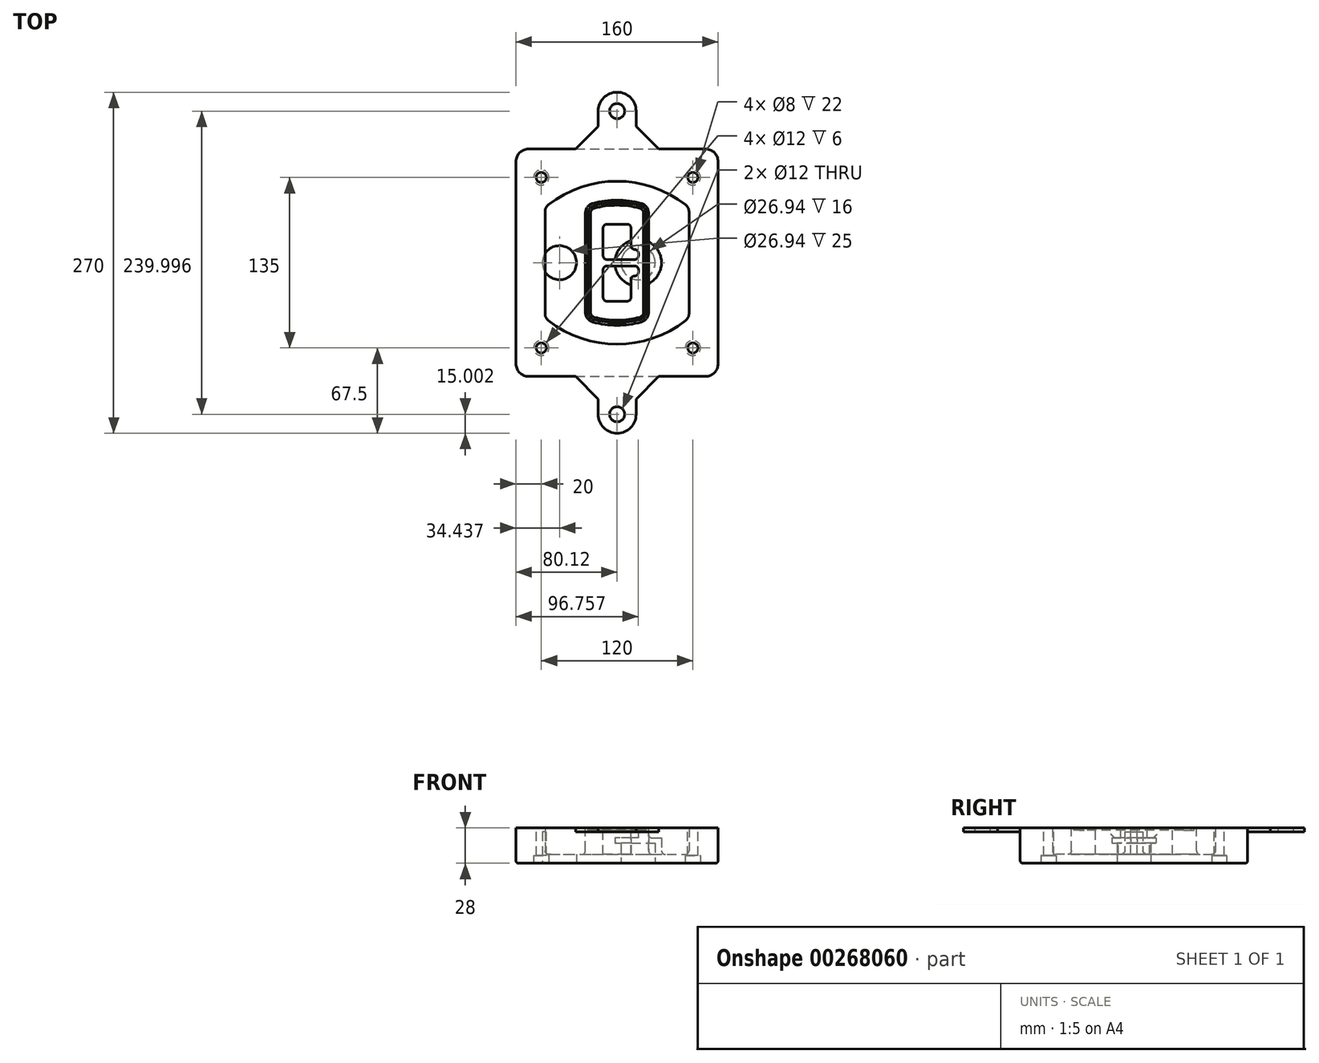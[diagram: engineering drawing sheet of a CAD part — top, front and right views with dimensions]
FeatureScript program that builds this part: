
annotation { "Feature Type Name" : "Feature", "Feature Type Description" : "" }
export const myFeature = defineFeature(function(context is Context, id is Id, definition is map)
    precondition{}
    {
        {
            var Q0;
            Q0=qCreatedBy(makeId("Top.planeOp"),FACE);
            var sketch = newSketch(context, id + "F0", { "sketchPlane" : qUnion([Q0])});
            skPoint(sketch, "E0.rect.middle", {"position": v(0, 0) * mm});
            skLineSegment(sketch, "E1.bottom", {"start": v(-70, -90) * mm, "end": v(70, -90) * mm});
            skLineSegment(sketch, "E1.top", {"start": v(-70, 90) * mm, "end": v(70, 90) * mm});
            skLineSegment(sketch, "E1.left", {"start": v(-80, -80) * mm, "end": v(-80, 80) * mm});
            skLineSegment(sketch, "E1.right", {"start": v(80, -80) * mm, "end": v(80, 80) * mm});
            skLineSegment(sketch, "E2", {"start": v(-80, 90) * mm, "end": v(80, -90) * mm, "construction": true});
            skLineSegment(sketch, "E3", {"start": v(80, 90) * mm, "end": v(-80, -90) * mm, "construction": true});
            skCircle(sketch, "E4", {"center": v(-60, 67.5) * mm, "radius": 4 * mm});
            skCircle(sketch, "E5", {"center": v(60, 67.5) * mm, "radius": 4 * mm});
            skCircle(sketch, "E6", {"center": v(60, -67.5) * mm, "radius": 4 * mm});
            skCircle(sketch, "E7", {"center": v(-60, -67.5) * mm, "radius": 4 * mm});
            skLineSegment(sketch, "E8", {"start": v(-60, 67.5) * mm, "end": v(60, 67.5) * mm, "construction": true});
            skLineSegment(sketch, "E9", {"start": v(60, 67.5) * mm, "end": v(60, -67.5) * mm, "construction": true});
            skLineSegment(sketch, "E10", {"start": v(60, -67.5) * mm, "end": v(-60, -67.5) * mm, "construction": true});
            skLineSegment(sketch, "E11", {"start": v(-60, -67.5) * mm, "end": v(-60, 67.5) * mm, "construction": true});
            skLineSegment(sketch, "E12", {"start": v(-60, 40.3) * mm, "end": v(-60, -40.3) * mm});
            skLineSegment(sketch, "E13", {"start": v(60, 40.3) * mm, "end": v(60, -40.3) * mm});
            skArc(sketch, "E14", {"start": v(56.15, 48.18) * mm, "mid": v(0, 67.5) * mm, "end": v(-56.15, 48.18) * mm});
            skArc(sketch, "E15", {"start": v(-56.15, -48.18) * mm, "mid": v(0, -67.5) * mm, "end": v(56.15, -48.18) * mm});
            skLineSegment(sketch, "E16", {"start": v(-60, 0) * mm, "end": v(60, 0) * mm, "construction": true});
            skPoint(sketch, "E17.visualSharp", {"position": v(-60, -45) * mm});
            skArc(sketch, "E17.filletArc", {"start": v(-60, -40.3) * mm, "mid": v(-58.99, -44.68) * mm, "end": v(-56.15, -48.18) * mm});
            skPoint(sketch, "E18.visualSharp", {"position": v(-60, 45) * mm});
            skArc(sketch, "E18.filletArc", {"start": v(-56.15, 48.18) * mm, "mid": v(-58.99, 44.68) * mm, "end": v(-60, 40.3) * mm});
            skPoint(sketch, "E19.visualSharp", {"position": v(60, 45) * mm});
            skArc(sketch, "E19.filletArc", {"start": v(60, 40.3) * mm, "mid": v(58.99, 44.68) * mm, "end": v(56.15, 48.18) * mm});
            skPoint(sketch, "E20.visualSharp", {"position": v(60, -45) * mm});
            skArc(sketch, "E20.filletArc", {"start": v(56.15, -48.18) * mm, "mid": v(58.99, -44.68) * mm, "end": v(60, -40.3) * mm});
            skPoint(sketch, "E21.visualSharp", {"position": v(-80, 90) * mm});
            skArc(sketch, "E21.filletArc", {"start": v(-70, 90) * mm, "mid": v(-77.07, 87.07) * mm, "end": v(-80, 80) * mm});
            skPoint(sketch, "E22.visualSharp", {"position": v(80, 90) * mm});
            skArc(sketch, "E22.filletArc", {"start": v(80, 80) * mm, "mid": v(77.07, 87.07) * mm, "end": v(70, 90) * mm});
            skPoint(sketch, "E23.visualSharp", {"position": v(80, -90) * mm});
            skArc(sketch, "E23.filletArc", {"start": v(70, -90) * mm, "mid": v(77.07, -87.07) * mm, "end": v(80, -80) * mm});
            skPoint(sketch, "E24.visualSharp", {"position": v(-80, -90) * mm});
            skArc(sketch, "E24.filletArc", {"start": v(-80, -80) * mm, "mid": v(-77.07, -87.07) * mm, "end": v(-70, -90) * mm});
            skArc(sketch, "E25.0", {"start": v(57, 40.3) * mm, "mid": v(56.3, 43.36) * mm, "end": v(54.3, 45.81) * mm});
            skLineSegment(sketch, "E25.1", {"start": v(57, 40.3) * mm, "end": v(57, -40.3) * mm});
            skArc(sketch, "E25.2", {"start": v(54.3, -45.81) * mm, "mid": v(56.3, -43.36) * mm, "end": v(57, -40.3) * mm});
            skArc(sketch, "E25.3", {"start": v(-54.3, -45.81) * mm, "mid": v(0, -64.5) * mm, "end": v(54.3, -45.81) * mm});
            skArc(sketch, "E25.4", {"start": v(-57, -40.3) * mm, "mid": v(-56.3, -43.36) * mm, "end": v(-54.3, -45.81) * mm});
            skArc(sketch, "E25.5", {"start": v(54.3, 45.81) * mm, "mid": v(0, 64.5) * mm, "end": v(-54.3, 45.81) * mm});
            skLineSegment(sketch, "E25.6", {"start": v(-57, 40.3) * mm, "end": v(-57, -40.3) * mm});
            skArc(sketch, "E25.7", {"start": v(-54.3, 45.81) * mm, "mid": v(-56.3, 43.36) * mm, "end": v(-57, 40.3) * mm});
            skArc(sketch, "E26.0", {"start": v(-58.62, 51.33) * mm, "mid": v(-62.58, 46.43) * mm, "end": v(-64, 40.3) * mm});
            skArc(sketch, "E26.1", {"start": v(58.62, 51.33) * mm, "mid": v(0, 71.5) * mm, "end": v(-58.62, 51.33) * mm});
            skArc(sketch, "E26.2", {"start": v(64, 40.3) * mm, "mid": v(62.58, 46.43) * mm, "end": v(58.62, 51.33) * mm});
            skLineSegment(sketch, "E26.3", {"start": v(64, 40.3) * mm, "end": v(64, -40.3) * mm});
            skArc(sketch, "E26.4", {"start": v(58.62, -51.33) * mm, "mid": v(62.58, -46.43) * mm, "end": v(64, -40.3) * mm});
            skLineSegment(sketch, "E26.5", {"start": v(-64, 40.3) * mm, "end": v(-64, -40.3) * mm});
            skArc(sketch, "E26.6", {"start": v(-58.62, -51.33) * mm, "mid": v(0, -71.5) * mm, "end": v(58.62, -51.33) * mm});
            skArc(sketch, "E26.7", {"start": v(-64, -40.3) * mm, "mid": v(-62.58, -46.43) * mm, "end": v(-58.62, -51.33) * mm});
            skSolve(sketch);
        }
        {
            var Q0;
            Q0=makeQuery(id+"F0.imprint","IMPRINT",FACE,{"disambiguationData":[TD([[makeQuery(id+"F0.imprint","IMPRINT",EDGE,{"derivedFrom":sQuery(id+"F0.wireOp",EDGE,"E1.bottom")}),1.0]])]});
            var Q1;
            Q1=makeQuery(id+"F0.imprint","IMPRINT",FACE,{"disambiguationData":[TD([[makeQuery(id+"F0.imprint","IMPRINT",EDGE,{"derivedFrom":sQuery(id+"F0.wireOp",EDGE,"E12")}),1.0]])]});
            var Q2;
            Q2=makeQuery(id+"F0.imprint","IMPRINT",FACE,{"disambiguationData":[TD([[makeQuery(id+"F0.imprint","IMPRINT",EDGE,{"derivedFrom":sQuery(id+"F0.wireOp",EDGE,"E25.0")}),1.0]])]});
            var Q3;
            Q3=makeQuery(id+"F0.imprint","IMPRINT",FACE,{"disambiguationData":[TD([[makeQuery(id+"F0.imprint","IMPRINT",EDGE,{"derivedFrom":sQuery(id+"F0.wireOp",EDGE,"E12")}),-1.0]])]});
            extrude(context, id + "F1", {"entities" : qUnion([Q0, Q1, Q2, Q3]), "oppositeDirection" : true, "depth" : 25 * mm});
        }
        {
            var Q0;
            Q0=makeQuery(id+"F0.imprint","IMPRINT",FACE,{"disambiguationData":[TD([[makeQuery(id+"F0.imprint","IMPRINT",EDGE,{"derivedFrom":sQuery(id+"F0.wireOp",EDGE,"E12")}),1.0]])]});
            extrude(context, id + "F2", {"entities" : qUnion([Q0]), "operationType" : NewBodyOperationType.ADD, "depth" : 3 * mm});
        }
        {
            var Q0;
            Q0=makeQuery(id+"F0.imprint","IMPRINT",FACE,{"disambiguationData":[TD([[makeQuery(id+"F0.imprint","IMPRINT",EDGE,{"derivedFrom":sQuery(id+"F0.wireOp",EDGE,"E25.0")}),1.0]])]});
            extrude(context, id + "F3", {"entities" : qUnion([Q0]), "operationType" : NewBodyOperationType.REMOVE, "oppositeDirection" : true, "depth" : 18 * mm});
        }
        {
            var Q0;
            Q0=makeQuery(id+"F2.opExtrude","CAP_FACE",FACE,{"disambiguationData":[OSD([sQuery(id+"F0.wireOp",EDGE,"E12"),sQuery(id+"F0.wireOp",EDGE,"E13"),sQuery(id+"F0.wireOp",EDGE,"E14"),sQuery(id+"F0.wireOp",EDGE,"E15"),sQuery(id+"F0.wireOp",EDGE,"E17.filletArc"),sQuery(id+"F0.wireOp",EDGE,"E18.filletArc"),sQuery(id+"F0.wireOp",EDGE,"E19.filletArc"),sQuery(id+"F0.wireOp",EDGE,"E20.filletArc"),sQuery(id+"F0.wireOp",EDGE,"E25.0"),sQuery(id+"F0.wireOp",EDGE,"E25.1"),sQuery(id+"F0.wireOp",EDGE,"E25.2"),sQuery(id+"F0.wireOp",EDGE,"E25.3"),sQuery(id+"F0.wireOp",EDGE,"E25.4"),sQuery(id+"F0.wireOp",EDGE,"E25.5"),sQuery(id+"F0.wireOp",EDGE,"E25.6"),sQuery(id+"F0.wireOp",EDGE,"E25.7")])],"isStart":false});
            var sketch = newSketch(context, id + "F4", { "sketchPlane" : qUnion([Q0])});
            skArc(sketch, "E27.0", {"start": v(-19.08, -46.97) * mm, "mid": v(0, -49.5) * mm, "end": v(19.08, -46.97) * mm});
            skArc(sketch, "E28.0", {"start": v(19.08, 46.97) * mm, "mid": v(0, 49.5) * mm, "end": v(-19.08, 46.97) * mm});
            skLineSegment(sketch, "E29", {"start": v(-25, 39.25) * mm, "end": v(-25, -39.25) * mm});
            skLineSegment(sketch, "E30", {"start": v(25, 39.25) * mm, "end": v(25, -39.25) * mm});
            skLineSegment(sketch, "E31", {"start": v(-25, 45.1) * mm, "end": v(25, 45.1) * mm, "construction": true});
            skLineSegment(sketch, "E32", {"start": v(-25, -45.1) * mm, "end": v(25, -45.1) * mm, "construction": true});
            skPoint(sketch, "E33.visualSharp", {"position": v(-25, 45.1) * mm});
            skArc(sketch, "E33.filletArc", {"start": v(-19.08, 46.97) * mm, "mid": v(-23.35, 44.11) * mm, "end": v(-25, 39.25) * mm});
            skPoint(sketch, "E34.visualSharp", {"position": v(25, 45.1) * mm});
            skArc(sketch, "E34.filletArc", {"start": v(25, 39.25) * mm, "mid": v(23.35, 44.11) * mm, "end": v(19.08, 46.97) * mm});
            skPoint(sketch, "E35.visualSharp", {"position": v(25, -45.1) * mm});
            skArc(sketch, "E35.filletArc", {"start": v(19.08, -46.97) * mm, "mid": v(23.35, -44.11) * mm, "end": v(25, -39.25) * mm});
            skPoint(sketch, "E36.visualSharp", {"position": v(-25, -45.1) * mm});
            skArc(sketch, "E36.filletArc", {"start": v(-25, -39.25) * mm, "mid": v(-23.35, -44.11) * mm, "end": v(-19.08, -46.97) * mm});
            skArc(sketch, "E37.0", {"start": v(54.3, 45.81) * mm, "mid": v(0, 64.5) * mm, "end": v(-54.3, 45.81) * mm});
            skArc(sketch, "E37.1", {"start": v(-54.3, 45.81) * mm, "mid": v(-56.3, 43.36) * mm, "end": v(-57, 40.3) * mm});
            skLineSegment(sketch, "E37.2", {"start": v(-57, 40.3) * mm, "end": v(-57, -40.3) * mm});
            skArc(sketch, "E37.3", {"start": v(-57, -40.3) * mm, "mid": v(-56.3, -43.36) * mm, "end": v(-54.3, -45.81) * mm});
            skArc(sketch, "E37.4", {"start": v(-54.3, -45.81) * mm, "mid": v(0, -64.5) * mm, "end": v(54.3, -45.81) * mm});
            skArc(sketch, "E37.5", {"start": v(54.3, -45.81) * mm, "mid": v(56.3, -43.36) * mm, "end": v(57, -40.3) * mm});
            skLineSegment(sketch, "E37.6", {"start": v(57, 40.3) * mm, "end": v(57, -40.3) * mm});
            skArc(sketch, "E37.7", {"start": v(57, 40.3) * mm, "mid": v(56.3, 43.36) * mm, "end": v(54.3, 45.81) * mm});
            skLineSegment(sketch, "E38.0", {"start": v(23, 39.25) * mm, "end": v(23, -39.25) * mm});
            skArc(sketch, "E38.1", {"start": v(18.56, -45.04) * mm, "mid": v(21.76, -42.9) * mm, "end": v(23, -39.25) * mm});
            skArc(sketch, "E38.2", {"start": v(-18.56, -45.04) * mm, "mid": v(0, -47.5) * mm, "end": v(18.56, -45.04) * mm});
            skArc(sketch, "E38.3", {"start": v(-23, -39.25) * mm, "mid": v(-21.76, -42.9) * mm, "end": v(-18.56, -45.04) * mm});
            skLineSegment(sketch, "E38.4", {"start": v(-23, 39.25) * mm, "end": v(-23, -39.25) * mm});
            skArc(sketch, "E38.5", {"start": v(23, 39.25) * mm, "mid": v(21.76, 42.9) * mm, "end": v(18.56, 45.04) * mm});
            skArc(sketch, "E38.6", {"start": v(-18.56, 45.04) * mm, "mid": v(-21.76, 42.9) * mm, "end": v(-23, 39.25) * mm});
            skArc(sketch, "E38.7", {"start": v(18.56, 45.04) * mm, "mid": v(0, 47.5) * mm, "end": v(-18.56, 45.04) * mm});
            skArc(sketch, "E39.0", {"start": v(21, 39.25) * mm, "mid": v(20.18, 41.68) * mm, "end": v(18.04, 43.1) * mm});
            skLineSegment(sketch, "E39.1", {"start": v(21, 39.25) * mm, "end": v(21, -39.25) * mm});
            skArc(sketch, "E39.2", {"start": v(18.04, -43.1) * mm, "mid": v(20.18, -41.68) * mm, "end": v(21, -39.25) * mm});
            skArc(sketch, "E39.3", {"start": v(-18.04, -43.1) * mm, "mid": v(0, -45.5) * mm, "end": v(18.04, -43.1) * mm});
            skArc(sketch, "E39.4", {"start": v(-21, -39.25) * mm, "mid": v(-20.18, -41.68) * mm, "end": v(-18.04, -43.1) * mm});
            skArc(sketch, "E39.5", {"start": v(18.04, 43.1) * mm, "mid": v(0, 45.5) * mm, "end": v(-18.04, 43.1) * mm});
            skLineSegment(sketch, "E39.6", {"start": v(-21, 39.25) * mm, "end": v(-21, -39.25) * mm});
            skArc(sketch, "E39.7", {"start": v(-18.04, 43.1) * mm, "mid": v(-20.18, 41.68) * mm, "end": v(-21, 39.25) * mm});
            skLineSegment(sketch, "E40", {"start": v(-25, 0) * mm, "end": v(25, 0) * mm, "construction": true});
            skLineSegment(sketch, "E41", {"start": v(-11, 5.5) * mm, "end": v(-11, 27.5) * mm});
            skLineSegment(sketch, "E42", {"start": v(-8, 30.5) * mm, "end": v(8, 30.5) * mm});
            skLineSegment(sketch, "E43", {"start": v(11, 27.5) * mm, "end": v(11, 13.5) * mm});
            skLineSegment(sketch, "E44", {"start": v(14, 10.5) * mm, "end": v(14, 10.5) * mm});
            skLineSegment(sketch, "E45", {"start": v(17, 7.5) * mm, "end": v(17, 5.5) * mm});
            skLineSegment(sketch, "E46", {"start": v(14, 2.5) * mm, "end": v(-8, 2.5) * mm});
            skPoint(sketch, "E47.visualSharp", {"position": v(-11, 30.5) * mm});
            skArc(sketch, "E47.filletArc", {"start": v(-8, 30.5) * mm, "mid": v(-10.12, 29.62) * mm, "end": v(-11, 27.5) * mm});
            skPoint(sketch, "E48.visualSharp", {"position": v(11, 30.5) * mm});
            skArc(sketch, "E48.filletArc", {"start": v(11, 27.5) * mm, "mid": v(10.12, 29.62) * mm, "end": v(8, 30.5) * mm});
            skPoint(sketch, "E49.visualSharp", {"position": v(11, 10.5) * mm});
            skArc(sketch, "E49.filletArc", {"start": v(11, 13.5) * mm, "mid": v(11.88, 11.38) * mm, "end": v(14, 10.5) * mm});
            skPoint(sketch, "E50.visualSharp", {"position": v(17, 10.5) * mm});
            skArc(sketch, "E50.filletArc", {"start": v(17, 7.5) * mm, "mid": v(16.12, 9.62) * mm, "end": v(14, 10.5) * mm});
            skPoint(sketch, "E51.visualSharp", {"position": v(17, 2.5) * mm});
            skArc(sketch, "E51.filletArc", {"start": v(14, 2.5) * mm, "mid": v(16.12, 3.38) * mm, "end": v(17, 5.5) * mm});
            skPoint(sketch, "E52.visualSharp", {"position": v(-11, 2.5) * mm});
            skArc(sketch, "E52.filletArc", {"start": v(-11, 5.5) * mm, "mid": v(-10.12, 3.38) * mm, "end": v(-8, 2.5) * mm});
            skLineSegment(sketch, "E53.0.MirrorCS", {"start": v(14, -2.5) * mm, "end": v(-8, -2.5) * mm});
            skArc(sketch, "E54.0.MirrorCS", {"start": v(-11, -5.5) * mm, "mid": v(-10.12, -3.38) * mm, "end": v(-8, -2.5) * mm});
            skLineSegment(sketch, "E55.0.MirrorCS", {"start": v(-11, -5.5) * mm, "end": v(-11, -27.5) * mm});
            skArc(sketch, "E56.0.MirrorCS", {"start": v(-8, -30.5) * mm, "mid": v(-10.12, -29.62) * mm, "end": v(-11, -27.5) * mm});
            skLineSegment(sketch, "E57.0.MirrorCS", {"start": v(-8, -30.5) * mm, "end": v(8, -30.5) * mm});
            skArc(sketch, "E58.0.MirrorCS", {"start": v(11, -27.5) * mm, "mid": v(10.12, -29.62) * mm, "end": v(8, -30.5) * mm});
            skLineSegment(sketch, "E59.0.MirrorCS", {"start": v(11, -27.5) * mm, "end": v(11, -13.5) * mm});
            skArc(sketch, "E60.0.MirrorCS", {"start": v(11, -13.5) * mm, "mid": v(11.88, -11.38) * mm, "end": v(14, -10.5) * mm});
            skArc(sketch, "E61.0.MirrorCS", {"start": v(17, -7.5) * mm, "mid": v(16.12, -9.62) * mm, "end": v(14, -10.5) * mm});
            skLineSegment(sketch, "E62.0.MirrorCS", {"start": v(17, -7.5) * mm, "end": v(17, -5.5) * mm});
            skArc(sketch, "E63.0.MirrorCS", {"start": v(14, -2.5) * mm, "mid": v(16.12, -3.38) * mm, "end": v(17, -5.5) * mm});
            skSolve(sketch);
        }
        {
            var Q0;
            Q0=makeQuery(id+"F4.imprint","IMPRINT",FACE,{"disambiguationData":[TD([[makeQuery(id+"F4.imprint","IMPRINT",EDGE,{"derivedFrom":sQuery(id+"F4.wireOp",EDGE,"E27.0")}),1.0]])]});
            var Q1;
            Q1=makeQuery(id+"F4.imprint","IMPRINT",FACE,{"disambiguationData":[TD([[makeQuery(id+"F4.imprint","IMPRINT",EDGE,{"derivedFrom":sQuery(id+"F4.wireOp",EDGE,"E38.0")}),-1.0]])]});
            var Q2;
            Q2=makeQuery(id+"F4.imprint","IMPRINT",FACE,{"disambiguationData":[TD([[makeQuery(id+"F4.imprint","IMPRINT",EDGE,{"derivedFrom":sQuery(id+"F4.wireOp",EDGE,"E39.0")}),1.0]])]});
            extrude(context, id + "F5", {"entities" : qUnion([Q0, Q1, Q2]), "operationType" : NewBodyOperationType.ADD, "endBound" : BoundingType.UP_TO_NEXT, "oppositeDirection" : true, "depth" : 25 * mm});
        }
        {
            var Q0;
            Q0=makeQuery(id+"F4.imprint","IMPRINT",FACE,{"disambiguationData":[TD([[makeQuery(id+"F4.imprint","IMPRINT",EDGE,{"derivedFrom":sQuery(id+"F4.wireOp",EDGE,"E38.0")}),-1.0]])]});
            extrude(context, id + "F6", {"entities" : qUnion([Q0]), "operationType" : NewBodyOperationType.REMOVE, "oppositeDirection" : true, "depth" : 2 * mm});
        }
        {
            var Q0;
            Q0=makeQuery(id+"F1.opExtrude","CAP_FACE",FACE,{"disambiguationData":[OSD([sQuery(id+"F0.wireOp",EDGE,"E1.bottom"),sQuery(id+"F0.wireOp",EDGE,"E1.top"),sQuery(id+"F0.wireOp",EDGE,"E1.left"),sQuery(id+"F0.wireOp",EDGE,"E1.right"),sQuery(id+"F0.wireOp",EDGE,"E4"),sQuery(id+"F0.wireOp",EDGE,"E5"),sQuery(id+"F0.wireOp",EDGE,"E6"),sQuery(id+"F0.wireOp",EDGE,"E7"),sQuery(id+"F0.wireOp",EDGE,"E21.filletArc"),sQuery(id+"F0.wireOp",EDGE,"E22.filletArc"),sQuery(id+"F0.wireOp",EDGE,"E23.filletArc"),sQuery(id+"F0.wireOp",EDGE,"E24.filletArc")])],"isStart":false});
            var sketch = newSketch(context, id + "F7", { "sketchPlane" : qUnion([Q0])});
            skCircle(sketch, "E64", {"center": v(16.76, 0) * mm, "radius": 13.47 * mm});
            skCircle(sketch, "E65", {"center": v(-45.56, 0) * mm, "radius": 13.47 * mm});
            skLineSegment(sketch, "E66", {"start": v(80, 0) * mm, "end": v(-80, 0) * mm});
            skCircle(sketch, "E67", {"center": v(16.76, 0) * mm, "radius": 18.47 * mm});
            skCircle(sketch, "E68", {"center": v(60, -67.5) * mm, "radius": 6 * mm});
            skCircle(sketch, "E69", {"center": v(-60, -67.5) * mm, "radius": 6 * mm});
            skCircle(sketch, "E70", {"center": v(-60, 67.5) * mm, "radius": 6 * mm});
            skCircle(sketch, "E71", {"center": v(60, 67.5) * mm, "radius": 6 * mm});
            skSolve(sketch);
        }
        {
            var Q0;
            {var subQ1=sQuery(id+"F7.wireOp",EDGE,"E66");var subQ4=sQuery(id+"F7.wireOp",EDGE,"E64");var subQ6=makeQuery(id+"F7.imprint","INTERSECT",VERTEX,{"disambiguationData":[OD(0.0)],"derivedFrom":[subQ4,subQ1]});Q0=makeQuery(id+"F7.imprint","IMPRINT",FACE,{"disambiguationData":[TD([[makeQuery(id+"F7.imprint","IMPRINT",EDGE,{"disambiguationData":[TD([[subQ6,-1.0]])],"derivedFrom":subQ4}),-1.0]])]});}
            var Q1;
            {var subQ0=sQuery(id+"F7.wireOp",EDGE,"E66");var subQ1=sQuery(id+"F7.wireOp",EDGE,"E64");var subQ3=makeQuery(id+"F7.imprint","INTERSECT",VERTEX,{"disambiguationData":[OD(0.0)],"derivedFrom":[subQ1,subQ0]});Q1=makeQuery(id+"F7.imprint","IMPRINT",FACE,{"disambiguationData":[TD([[makeQuery(id+"F7.imprint","IMPRINT",EDGE,{"disambiguationData":[TD([[subQ3,-1.0]])],"derivedFrom":subQ1}),1.0]])]});}
            var Q2;
            {var subQ0=sQuery(id+"F7.wireOp",EDGE,"E66");var subQ1=sQuery(id+"F7.wireOp",EDGE,"E64");var subQ3=makeQuery(id+"F7.imprint","INTERSECT",VERTEX,{"disambiguationData":[OD(0.0)],"derivedFrom":[subQ1,subQ0]});Q2=makeQuery(id+"F7.imprint","IMPRINT",FACE,{"disambiguationData":[TD([[makeQuery(id+"F7.imprint","IMPRINT",EDGE,{"disambiguationData":[TD([[subQ3,1.0]])],"derivedFrom":subQ1}),1.0]])]});}
            var Q3;
            {var subQ1=sQuery(id+"F7.wireOp",EDGE,"E66");var subQ4=sQuery(id+"F7.wireOp",EDGE,"E64");var subQ6=makeQuery(id+"F7.imprint","INTERSECT",VERTEX,{"disambiguationData":[OD(0.0)],"derivedFrom":[subQ4,subQ1]});Q3=makeQuery(id+"F7.imprint","IMPRINT",FACE,{"disambiguationData":[TD([[makeQuery(id+"F7.imprint","IMPRINT",EDGE,{"disambiguationData":[TD([[subQ6,1.0]])],"derivedFrom":subQ4}),-1.0]])]});}
            extrude(context, id + "F8", {"entities" : qUnion([Q0, Q1, Q2, Q3]), "operationType" : NewBodyOperationType.ADD, "oppositeDirection" : true, "depth" : 20 * mm});
        }
        {
            var Q0;
            {var subQ0=sQuery(id+"F7.wireOp",EDGE,"E66");var subQ1=sQuery(id+"F7.wireOp",EDGE,"E64");var subQ3=makeQuery(id+"F7.imprint","INTERSECT",VERTEX,{"disambiguationData":[OD(0.0)],"derivedFrom":[subQ1,subQ0]});Q0=makeQuery(id+"F7.imprint","IMPRINT",FACE,{"disambiguationData":[TD([[makeQuery(id+"F7.imprint","IMPRINT",EDGE,{"disambiguationData":[TD([[subQ3,-1.0]])],"derivedFrom":subQ1}),1.0]])]});}
            var Q1;
            {var subQ0=sQuery(id+"F7.wireOp",EDGE,"E66");var subQ1=sQuery(id+"F7.wireOp",EDGE,"E64");var subQ3=makeQuery(id+"F7.imprint","INTERSECT",VERTEX,{"disambiguationData":[OD(0.0)],"derivedFrom":[subQ1,subQ0]});Q1=makeQuery(id+"F7.imprint","IMPRINT",FACE,{"disambiguationData":[TD([[makeQuery(id+"F7.imprint","IMPRINT",EDGE,{"disambiguationData":[TD([[subQ3,1.0]])],"derivedFrom":subQ1}),1.0]])]});}
            extrude(context, id + "F9", {"entities" : qUnion([Q0, Q1]), "operationType" : NewBodyOperationType.REMOVE, "oppositeDirection" : true, "depth" : 16 * mm});
        }
        {
            var Q0;
            {var subQ0=sQuery(id+"F7.wireOp",EDGE,"E66");var subQ1=sQuery(id+"F7.wireOp",EDGE,"E65");var subQ3=makeQuery(id+"F7.imprint","INTERSECT",VERTEX,{"disambiguationData":[OD(0.0)],"derivedFrom":[subQ1,subQ0]});Q0=makeQuery(id+"F7.imprint","IMPRINT",FACE,{"disambiguationData":[TD([[makeQuery(id+"F7.imprint","IMPRINT",EDGE,{"disambiguationData":[TD([[subQ3,-1.0]])],"derivedFrom":subQ1}),1.0]])]});}
            var Q1;
            {var subQ0=sQuery(id+"F7.wireOp",EDGE,"E66");var subQ1=sQuery(id+"F7.wireOp",EDGE,"E65");var subQ3=makeQuery(id+"F7.imprint","INTERSECT",VERTEX,{"disambiguationData":[OD(0.0)],"derivedFrom":[subQ1,subQ0]});Q1=makeQuery(id+"F7.imprint","IMPRINT",FACE,{"disambiguationData":[TD([[makeQuery(id+"F7.imprint","IMPRINT",EDGE,{"disambiguationData":[TD([[subQ3,1.0]])],"derivedFrom":subQ1}),1.0]])]});}
            extrude(context, id + "F10", {"entities" : qUnion([Q0, Q1]), "operationType" : NewBodyOperationType.REMOVE, "oppositeDirection" : true, "depth" : 25 * mm});
        }
        {
            var Q0;
            Q0=makeQuery(id+"F7.imprint","IMPRINT",FACE,{"disambiguationData":[TD([[makeQuery(id+"F7.imprint","IMPRINT",EDGE,{"derivedFrom":sQuery(id+"F7.wireOp",EDGE,"E68")}),1.0]])]});
            var Q1;
            Q1=makeQuery(id+"F7.imprint","IMPRINT",FACE,{"disambiguationData":[TD([[makeQuery(id+"F7.imprint","IMPRINT",EDGE,{"derivedFrom":makeQuery(id+"F1.opExtrude","CAP_EDGE",EDGE,{"disambiguationData":[OSD([sQuery(id+"F0.wireOp",EDGE,"E5")])],"isStart":false})}),-1.0]])]});
            var Q2;
            Q2=makeQuery(id+"F7.imprint","IMPRINT",FACE,{"disambiguationData":[TD([[makeQuery(id+"F7.imprint","IMPRINT",EDGE,{"derivedFrom":sQuery(id+"F7.wireOp",EDGE,"E69")}),1.0]])]});
            var Q3;
            Q3=makeQuery(id+"F7.imprint","IMPRINT",FACE,{"disambiguationData":[TD([[makeQuery(id+"F7.imprint","IMPRINT",EDGE,{"derivedFrom":makeQuery(id+"F1.opExtrude","CAP_EDGE",EDGE,{"disambiguationData":[OSD([sQuery(id+"F0.wireOp",EDGE,"E4")])],"isStart":false})}),-1.0]])]});
            var Q4;
            Q4=makeQuery(id+"F7.imprint","IMPRINT",FACE,{"disambiguationData":[TD([[makeQuery(id+"F7.imprint","IMPRINT",EDGE,{"derivedFrom":sQuery(id+"F7.wireOp",EDGE,"E70")}),1.0]])]});
            var Q5;
            Q5=makeQuery(id+"F7.imprint","IMPRINT",FACE,{"disambiguationData":[TD([[makeQuery(id+"F7.imprint","IMPRINT",EDGE,{"derivedFrom":makeQuery(id+"F1.opExtrude","CAP_EDGE",EDGE,{"disambiguationData":[OSD([sQuery(id+"F0.wireOp",EDGE,"E7")])],"isStart":false})}),-1.0]])]});
            var Q6;
            Q6=makeQuery(id+"F7.imprint","IMPRINT",FACE,{"disambiguationData":[TD([[makeQuery(id+"F7.imprint","IMPRINT",EDGE,{"derivedFrom":sQuery(id+"F7.wireOp",EDGE,"E71")}),1.0]])]});
            var Q7;
            Q7=makeQuery(id+"F7.imprint","IMPRINT",FACE,{"disambiguationData":[TD([[makeQuery(id+"F7.imprint","IMPRINT",EDGE,{"derivedFrom":makeQuery(id+"F1.opExtrude","CAP_EDGE",EDGE,{"disambiguationData":[OSD([sQuery(id+"F0.wireOp",EDGE,"E6")])],"isStart":false})}),-1.0]])]});
            extrude(context, id + "F11", {"entities" : qUnion([Q0, Q1, Q2, Q3, Q4, Q5, Q6, Q7]), "operationType" : NewBodyOperationType.REMOVE, "oppositeDirection" : true, "depth" : 6 * mm});
        }
        {
            var Q0;
            Q0=makeQuery(id+"F9.boolean.opBoolean","COPY",FACE,{"derivedFrom":makeQuery(id+"F9.opExtrude","CAP_FACE",FACE,{"disambiguationData":[OSD([sQuery(id+"F7.wireOp",EDGE,"E64")])],"isStart":false})});
            var sketch = newSketch(context, id + "F12", { "sketchPlane" : qUnion([Q0])});
            skArc(sketch, "E72.0", {"start": v(11, 17.55) * mm, "mid": v(2.57, 11.82) * mm, "end": v(-1.54, 2.5) * mm});
            skArc(sketch, "E72.1", {"start": v(-1.54, -2.5) * mm, "mid": v(2.57, -11.82) * mm, "end": v(11, -17.55) * mm});
            skLineSegment(sketch, "E73", {"start": v(-1.54, -2.5) * mm, "end": v(14, -2.5) * mm});
            skLineSegment(sketch, "E74.0", {"start": v(14, 2.5) * mm, "end": v(-1.54, 2.5) * mm});
            skArc(sketch, "E74.1", {"start": v(14, 2.5) * mm, "mid": v(16.12, 3.38) * mm, "end": v(17, 5.5) * mm});
            skLineSegment(sketch, "E74.2", {"start": v(17, 7.5) * mm, "end": v(17, 5.5) * mm});
            skArc(sketch, "E74.3", {"start": v(17, 7.5) * mm, "mid": v(16.12, 9.62) * mm, "end": v(14, 10.5) * mm});
            skArc(sketch, "E74.4", {"start": v(11, 13.5) * mm, "mid": v(11.88, 11.38) * mm, "end": v(14, 10.5) * mm});
            skLineSegment(sketch, "E74.5", {"start": v(11, 17.55) * mm, "end": v(11, 13.5) * mm});
            skLineSegment(sketch, "E74.7", {"start": v(14, -2.5) * mm, "end": v(-1.54, -2.5) * mm});
            skArc(sketch, "E74.8", {"start": v(14, -2.5) * mm, "mid": v(16.12, -3.38) * mm, "end": v(17, -5.5) * mm});
            skLineSegment(sketch, "E74.9", {"start": v(17, -7.5) * mm, "end": v(17, -5.5) * mm});
            skArc(sketch, "E74.10", {"start": v(17, -7.5) * mm, "mid": v(16.12, -9.62) * mm, "end": v(14, -10.5) * mm});
            skArc(sketch, "E74.11", {"start": v(11, -13.5) * mm, "mid": v(11.88, -11.38) * mm, "end": v(14, -10.5) * mm});
            skLineSegment(sketch, "E74.12", {"start": v(11, -17.55) * mm, "end": v(11, -13.5) * mm});
            skPoint(sketch, "E75.orphan", {"position": v(11, -27.5) * mm});
            skPoint(sketch, "E76.orphan", {"position": v(-8, -2.5) * mm});
            skPoint(sketch, "E77.orphan", {"position": v(-8, 2.5) * mm});
            skPoint(sketch, "E78.orphan", {"position": v(11, 27.5) * mm});
            skSolve(sketch);
        }
        {
            var Q0;
            {var subQ7=sQuery(id+"F12.wireOp",EDGE,"E72.0");var subQ14=sQuery(id+"F12.wireOp",EDGE,"E72.1");var subQ16=sQuery(id+"F12.wireOp",EDGE,"E74.1");var subQ18=sQuery(id+"F12.wireOp",EDGE,"E74.8");Q0=qUnion([makeQuery(id+"F12.imprint","IMPRINT",FACE,{"disambiguationData":[TD([[makeQuery(id+"F12.imprint","IMPRINT",EDGE,{"derivedFrom":subQ7}),1.0]])]}),makeQuery(id+"F12.imprint","IMPRINT",FACE,{"disambiguationData":[TD([[makeQuery(id+"F12.imprint","IMPRINT",EDGE,{"derivedFrom":subQ14}),1.0]])]}),makeQuery(id+"F12.imprint","IMPRINT",FACE,{"disambiguationData":[TD([[makeQuery(id+"F12.imprint","IMPRINT",EDGE,{"derivedFrom":subQ16}),1.0]])]}),makeQuery(id+"F12.imprint","IMPRINT",FACE,{"disambiguationData":[TD([[makeQuery(id+"F12.imprint","IMPRINT",EDGE,{"derivedFrom":subQ18}),-1.0]])]})]);}
            var Q1;
            Q1=makeQuery(id+"F5.boolean.opBoolean","SPLIT",FACE,{"disambiguationData":[TD([makeQuery(id+"F5.opExtrude","SWEPT_FACE",FACE,{"disambiguationData":[OSD([sQuery(id+"F4.wireOp",EDGE,"E41")])]})])],"derivedFrom":makeQuery(id+"F3.boolean.opBoolean","COPY",FACE,{"derivedFrom":makeQuery(id+"F3.opExtrude","CAP_FACE",FACE,{"disambiguationData":[OSD([sQuery(id+"F0.wireOp",EDGE,"E25.0"),sQuery(id+"F0.wireOp",EDGE,"E25.1"),sQuery(id+"F0.wireOp",EDGE,"E25.2"),sQuery(id+"F0.wireOp",EDGE,"E25.3"),sQuery(id+"F0.wireOp",EDGE,"E25.4"),sQuery(id+"F0.wireOp",EDGE,"E25.5"),sQuery(id+"F0.wireOp",EDGE,"E25.6"),sQuery(id+"F0.wireOp",EDGE,"E25.7")])],"isStart":false})})});
            extrude(context, id + "F13", {"entities" : qUnion([Q0]), "operationType" : NewBodyOperationType.REMOVE, "endBound" : BoundingType.UP_TO_SURFACE, "endBoundEntityFace" : qUnion([Q1]), "depth" : 25 * mm});
        }
        {
            var Q0;
            Q0=makeQuery(id+"F3.boolean.opBoolean","COPY",EDGE,{"derivedFrom":makeQuery(id+"F3.opExtrude","CAP_EDGE",EDGE,{"disambiguationData":[OSD([sQuery(id+"F0.wireOp",EDGE,"E25.6")])],"isStart":false})});
            var Q1;
            Q1=makeQuery(id+"F8.boolean.opBoolean","INTERSECT",EDGE,{"derivedFrom":[makeQuery(id+"F5.opExtrude","SWEPT_FACE",FACE,{"disambiguationData":[OSD([sQuery(id+"F4.wireOp",EDGE,"E30")])]}),makeQuery(id+"F8.opExtrude","CAP_FACE",FACE,{"disambiguationData":[OSD([sQuery(id+"F7.wireOp",EDGE,"E67")])],"isStart":false})]});
            var Q2;
            Q2=makeQuery(id+"F8.boolean.opBoolean","INTERSECT",EDGE,{"disambiguationData":[OD(1.0)],"derivedFrom":[makeQuery(id+"F5.opExtrude","SWEPT_FACE",FACE,{"disambiguationData":[OSD([sQuery(id+"F4.wireOp",EDGE,"E30")])]}),makeQuery(id+"F8.opExtrude","SWEPT_FACE",FACE,{"disambiguationData":[OSD([sQuery(id+"F7.wireOp",EDGE,"E67")])]})]});
            var Q3;
            {var subQ0=sQuery(id+"F4.wireOp",EDGE,"E30");Q3=makeQuery(id+"F8.boolean.opBoolean","SPLIT",EDGE,{"disambiguationData":[TD([makeQuery(id+"F5.opExtrude","SWEPT_FACE",FACE,{"disambiguationData":[OSD([sQuery(id+"F4.wireOp",EDGE,"E35.filletArc")])]})])],"derivedFrom":makeQuery(id+"F5.opExtrude","CAP_EDGE",EDGE,{"disambiguationData":[OSD([subQ0])],"isStart":false})});}
            var Q4;
            {var subQ0=sQuery(id+"F0.wireOp",EDGE,"E25.7");var subQ1=sQuery(id+"F0.wireOp",EDGE,"E25.1");var subQ2=sQuery(id+"F0.wireOp",EDGE,"E25.6");var subQ3=sQuery(id+"F0.wireOp",EDGE,"E25.5");var subQ4=sQuery(id+"F0.wireOp",EDGE,"E25.4");var subQ5=sQuery(id+"F0.wireOp",EDGE,"E25.0");var subQ6=sQuery(id+"F0.wireOp",EDGE,"E25.2");var subQ7=sQuery(id+"F0.wireOp",EDGE,"E25.3");Q4=makeQuery(id+"F8.boolean.opBoolean","INTERSECT",EDGE,{"derivedFrom":[makeQuery(id+"F5.boolean.opBoolean","SPLIT",FACE,{"disambiguationData":[TD([makeQuery(id+"F2.opExtrude","SWEPT_FACE",FACE,{"disambiguationData":[OSD([subQ5])]})])],"derivedFrom":makeQuery(id+"F3.boolean.opBoolean","COPY",FACE,{"derivedFrom":makeQuery(id+"F3.opExtrude","CAP_FACE",FACE,{"disambiguationData":[OSD([subQ5,subQ1,subQ6,subQ7,subQ4,subQ3,subQ2,subQ0])],"isStart":false})})}),makeQuery(id+"F8.opExtrude","SWEPT_FACE",FACE,{"disambiguationData":[OSD([sQuery(id+"F7.wireOp",EDGE,"E67")])]})]});}
            var Q5;
            Q5=makeQuery(id+"F8.boolean.opBoolean","INTERSECT",EDGE,{"disambiguationData":[OD(0.0)],"derivedFrom":[makeQuery(id+"F5.opExtrude","SWEPT_FACE",FACE,{"disambiguationData":[OSD([sQuery(id+"F4.wireOp",EDGE,"E30")])]}),makeQuery(id+"F8.opExtrude","SWEPT_FACE",FACE,{"disambiguationData":[OSD([sQuery(id+"F7.wireOp",EDGE,"E67")])]})]});
            fillet(context, id + "F14", {"entities" : qUnion([Q0, Q1, Q2, Q3, Q4, Q5]), "radius" : 3 * mm, "tangentPropagation" : true, "allowEdgeOverflow" : false});
        }
        {
            var Q0;
            Q0=makeQuery(id+"F1.opExtrude","CAP_EDGE",EDGE,{"disambiguationData":[OSD([sQuery(id+"F0.wireOp",EDGE,"E1.bottom")])],"isStart":false});
            fillet(context, id + "F15", {"entities" : qUnion([Q0]), "radius" : 2 * mm, "tangentPropagation" : true, "allowEdgeOverflow" : false});
        }
        {
            var Q0;
            {var subQ0=sQuery(id+"F0.wireOp",EDGE,"E22.filletArc");var subQ1=sQuery(id+"F0.wireOp",EDGE,"E7");var subQ2=sQuery(id+"F0.wireOp",EDGE,"E6");var subQ3=sQuery(id+"F0.wireOp",EDGE,"E5");var subQ4=sQuery(id+"F0.wireOp",EDGE,"E4");var subQ5=sQuery(id+"F0.wireOp",EDGE,"E1.bottom");var subQ6=sQuery(id+"F0.wireOp",EDGE,"E21.filletArc");var subQ7=sQuery(id+"F0.wireOp",EDGE,"E1.top");var subQ8=sQuery(id+"F0.wireOp",EDGE,"E1.left");var subQ9=sQuery(id+"F0.wireOp",EDGE,"E1.right");var subQ10=sQuery(id+"F0.wireOp",EDGE,"E23.filletArc");var subQ11=sQuery(id+"F0.wireOp",EDGE,"E24.filletArc");Q0=makeQuery(id+"F2.boolean.opBoolean","SPLIT",FACE,{"disambiguationData":[TD([makeQuery(id+"F1.opExtrude","SWEPT_FACE",FACE,{"disambiguationData":[OSD([subQ5])]})])],"derivedFrom":makeQuery(id+"F1.opExtrude","CAP_FACE",FACE,{"disambiguationData":[OSD([subQ5,subQ7,subQ8,subQ9,subQ4,subQ3,subQ2,subQ1,subQ6,subQ0,subQ10,subQ11])],"isStart":true})});}
            var sketch = newSketch(context, id + "F16", { "sketchPlane" : qUnion([Q0])});
            skLineSegment(sketch, "E79", {"start": v(-32.88, 90) * mm, "end": v(-14.88, 108) * mm});
            skLineSegment(sketch, "E80", {"start": v(-14.88, 108) * mm, "end": v(-14.88, 120) * mm});
            skLineSegment(sketch, "E81", {"start": v(33.12, 90) * mm, "end": v(15.12, 108) * mm});
            skLineSegment(sketch, "E82", {"start": v(15.12, 108) * mm, "end": v(15.12, 120) * mm});
            skArc(sketch, "E83", {"start": v(15.12, 120) * mm, "mid": v(0.12, 135) * mm, "end": v(-14.88, 120) * mm});
            skLineSegment(sketch, "E84", {"start": v(-0.22, 90) * mm, "end": v(0.12, 120) * mm, "construction": true});
            skCircle(sketch, "E85", {"center": v(0.12, 120) * mm, "radius": 6 * mm});
            skLineSegment(sketch, "E86", {"start": v(-80, 0) * mm, "end": v(80, 0) * mm, "construction": true});
            skLineSegment(sketch, "E87.MirrorCS", {"start": v(-32.88, -90) * mm, "end": v(-14.88, -108) * mm});
            skLineSegment(sketch, "E88.MirrorCS", {"start": v(-14.88, -108) * mm, "end": v(-14.88, -120) * mm});
            skArc(sketch, "E89.MirrorCS", {"start": v(15.12, -120) * mm, "mid": v(0.12, -135) * mm, "end": v(-14.88, -120) * mm});
            skCircle(sketch, "E90.MirrorC", {"center": v(0.12, -120) * mm, "radius": 6 * mm});
            skLineSegment(sketch, "E91.MirrorCS", {"start": v(15.12, -108) * mm, "end": v(15.12, -120) * mm});
            skLineSegment(sketch, "E92.MirrorCS", {"start": v(33.12, -90) * mm, "end": v(15.12, -108) * mm});
            skSolve(sketch);
        }
        {
            var Q0;
            {var subQ1=sQuery(id+"F16.wireOp",EDGE,"E79");Q0=makeQuery(id+"F16.imprint","IMPRINT",FACE,{"disambiguationData":[TD([[makeQuery(id+"F16.imprint","IMPRINT",EDGE,{"derivedFrom":subQ1}),-1.0]])]});}
            var Q1;
            {var subQ0=sQuery(id+"F16.wireOp",EDGE,"E87.MirrorCS");Q1=makeQuery(id+"F16.imprint","IMPRINT",FACE,{"disambiguationData":[TD([[makeQuery(id+"F16.imprint","IMPRINT",EDGE,{"derivedFrom":subQ0}),1.0]])]});}
            var Q2;
            Q2=makeQuery(id+"F16.imprint","IMPRINT",FACE,{"disambiguationData":[TD([[makeQuery(id+"F16.imprint","IMPRINT",EDGE,{"derivedFrom":makeQuery(id+"F1.opExtrude","CAP_EDGE",EDGE,{"disambiguationData":[OSD([sQuery(id+"F0.wireOp",EDGE,"E1.left")])],"isStart":true})}),-1.0]])]});
            var Q3;
            Q3=makeQuery(id+"F2.opExtrude","CAP_FACE",FACE,{"disambiguationData":[OSD([sQuery(id+"F0.wireOp",EDGE,"E12"),sQuery(id+"F0.wireOp",EDGE,"E13"),sQuery(id+"F0.wireOp",EDGE,"E14"),sQuery(id+"F0.wireOp",EDGE,"E15"),sQuery(id+"F0.wireOp",EDGE,"E17.filletArc"),sQuery(id+"F0.wireOp",EDGE,"E18.filletArc"),sQuery(id+"F0.wireOp",EDGE,"E19.filletArc"),sQuery(id+"F0.wireOp",EDGE,"E20.filletArc"),sQuery(id+"F0.wireOp",EDGE,"E25.0"),sQuery(id+"F0.wireOp",EDGE,"E25.1"),sQuery(id+"F0.wireOp",EDGE,"E25.2"),sQuery(id+"F0.wireOp",EDGE,"E25.3"),sQuery(id+"F0.wireOp",EDGE,"E25.4"),sQuery(id+"F0.wireOp",EDGE,"E25.5"),sQuery(id+"F0.wireOp",EDGE,"E25.6"),sQuery(id+"F0.wireOp",EDGE,"E25.7")])],"isStart":false});
            extrude(context, id + "F17", {"entities" : qUnion([Q0, Q1, Q2]), "operationType" : NewBodyOperationType.ADD, "endBound" : BoundingType.UP_TO_SURFACE, "endBoundEntityFace" : qUnion([Q3]), "depth" : 25 * mm});
        }
    });
